FCSTD DOCUMENT  (FreeCAD 0.18.4R)
Label: carro-impresso
License: All rights reserved
LicenseURL: http://en.wikipedia.org/wiki/All_rights_reserved
objects: Sketcher::SketchObject×1, PartDesign::Body×1
note: 2 computed .brp shape members not serialized (recipe doc carries the construction recipe); baked Part::Feature solids carry a one-line shape summary decoded from their .brp

FEATURE [Sketcher::SketchObject] Sketch
  MapMode = 5
  Support = -> [XY_Plane]
  sketch-geometry (35):
    g0: LineSegment StartX=-22.5 StartY=-27.5 StartZ=0 EndX=22.5 EndY=-27.5 EndZ=0
    g1: LineSegment StartX=27.5 StartY=-22.5 StartZ=0 EndX=27.5 EndY=22.5 EndZ=0
    g2: LineSegment StartX=22.5 StartY=27.5 StartZ=0 EndX=-22.5 EndY=27.5 EndZ=0
    g3: LineSegment StartX=-27.5 StartY=22.5 StartZ=0 EndX=-27.5 EndY=-22.5 EndZ=0
    g4: ArcOfCircle CenterX=22.5 CenterY=22.5 CenterZ=0 NormalX=0 NormalY=0 NormalZ=1 AngleXU=0 Radius=5 StartAngle=0 EndAngle=1.5708
    g5: ArcOfCircle CenterX=-22.5 CenterY=22.5 CenterZ=0 NormalX=0 NormalY=0 NormalZ=1 AngleXU=0 Radius=5 StartAngle=1.5708 EndAngle=3.14159
    g6: ArcOfCircle CenterX=-22.5 CenterY=-22.5 CenterZ=0 NormalX=0 NormalY=0 NormalZ=1 AngleXU=0 Radius=5 StartAngle=3.14159 EndAngle=4.71239
    g7: ArcOfCircle CenterX=22.5 CenterY=-22.5 CenterZ=0 NormalX=0 NormalY=0 NormalZ=1 AngleXU=0 Radius=5 StartAngle=4.71239 EndAngle=6.28319
    g8: Circle CenterX=-20 CenterY=20 CenterZ=0 NormalX=0 NormalY=0 NormalZ=1 AngleXU=0 Radius=3
    g9: Circle CenterX=20 CenterY=20 CenterZ=0 NormalX=0 NormalY=0 NormalZ=1 AngleXU=0 Radius=3
    g10: Circle CenterX=0 CenterY=-20 CenterZ=0 NormalX=0 NormalY=0 NormalZ=1 AngleXU=0 Radius=3
    g11: LineSegment [constr] StartX=-27.5 StartY=20 StartZ=0 EndX=27.5 EndY=20 EndZ=0
    g12: Circle CenterX=20 CenterY=-20 CenterZ=0 NormalX=0 NormalY=0 NormalZ=1 AngleXU=0 Radius=1.5
    g13: Circle CenterX=20 CenterY=0 CenterZ=0 NormalX=0 NormalY=0 NormalZ=1 AngleXU=0 Radius=1.5
    g14: Circle CenterX=10 CenterY=20 CenterZ=0 NormalX=0 NormalY=0 NormalZ=1 AngleXU=0 Radius=1.5
    g15: Circle CenterX=10 CenterY=0 CenterZ=0 NormalX=0 NormalY=0 NormalZ=1 AngleXU=0 Radius=1.5
    g16: Circle CenterX=-10 CenterY=20 CenterZ=0 NormalX=0 NormalY=0 NormalZ=1 AngleXU=0 Radius=1.5
    g17: Circle CenterX=-10 CenterY=0 CenterZ=0 NormalX=0 NormalY=0 NormalZ=1 AngleXU=0 Radius=1.5
    g18: Circle CenterX=-20 CenterY=-20 CenterZ=0 NormalX=0 NormalY=0 NormalZ=1 AngleXU=0 Radius=1.5
    g19: Circle CenterX=-20 CenterY=0 CenterZ=0 NormalX=0 NormalY=0 NormalZ=1 AngleXU=0 Radius=1.5
    g20: LineSegment [constr] StartX=-10 StartY=27.5 StartZ=0 EndX=-10 EndY=-27.5 EndZ=0
    g21: LineSegment [constr] StartX=-20 StartY=27.5 StartZ=0 EndX=-20 EndY=-27.5 EndZ=0
    g22: LineSegment [constr] StartX=-27.5 StartY=-20 StartZ=0 EndX=27.5 EndY=-20 EndZ=0
    g23: LineSegment [constr] StartX=10 StartY=27.5 StartZ=0 EndX=10 EndY=-27.5 EndZ=0
    g24: LineSegment [constr] StartX=20 StartY=27.5 StartZ=0 EndX=20 EndY=-27.5 EndZ=0
    g25: LineSegment [constr] StartX=-27.5 StartY=-10 StartZ=0 EndX=27.5 EndY=-10 EndZ=0
    g26: LineSegment [constr] StartX=-27.5 StartY=10 StartZ=0 EndX=27.5 EndY=10 EndZ=0
    g27: Circle CenterX=-20 CenterY=10 CenterZ=0 NormalX=0 NormalY=0 NormalZ=1 AngleXU=0 Radius=1.5
    g28: Circle CenterX=-10 CenterY=10 CenterZ=0 NormalX=0 NormalY=0 NormalZ=1 AngleXU=0 Radius=1.5
    g29: Circle CenterX=10 CenterY=10 CenterZ=0 NormalX=0 NormalY=0 NormalZ=1 AngleXU=0 Radius=1.5
    g30: Circle CenterX=20 CenterY=10 CenterZ=0 NormalX=0 NormalY=0 NormalZ=1 AngleXU=0 Radius=1.5
    g31: Circle CenterX=10 CenterY=-10 CenterZ=0 NormalX=0 NormalY=0 NormalZ=1 AngleXU=0 Radius=1.5
    g32: Circle CenterX=-10 CenterY=-10 CenterZ=0 NormalX=0 NormalY=0 NormalZ=1 AngleXU=0 Radius=1.5
    g33: Circle CenterX=-20 CenterY=-10 CenterZ=0 NormalX=0 NormalY=0 NormalZ=1 AngleXU=0 Radius=1.5
    g34: Circle CenterX=20 CenterY=-10 CenterZ=0 NormalX=0 NormalY=0 NormalZ=1 AngleXU=0 Radius=1.5
  constraints (100):
    c: Horizontal(g0)
    c: Horizontal(g2)
    c: Vertical(g1)
    c: Vertical(g3)
    c: Tangent(g2,g4) = -1.5708
    c: Tangent(g1,g4) = -1.5708
    c: Tangent(g2,g5) = -1.5708
    c: Tangent(g3,g5) = -1.5708
    c: Tangent(g3,g6) = -1.5708
    c: Tangent(g0,g6) = -1.5708
    c: Tangent(g1,g7) = -1.5708
    c: Tangent(g0,g7) = -1.5708
    c: Equal(g5,g6)
    c: Equal(g6,g7)
    c: Equal(g7,g4)
    c: Symmetric(g7,g5,g-1)
    c: DistanceX(g3,g1) = 55
    c: DistanceY(g0,g2) = 55
    c: Diameter(g5) = 10
    c: PointOnObject(g10,g-2)
    c: Diameter(g10) = 6
    c: Diameter(g8) = 6
    c: Diameter(g9) = 6
    c: Horizontal(g11)
    c: PointOnObject(g8,g11)
    c: PointOnObject(g9,g11)
    c: PointOnObject(g11,g3)
    c: PointOnObject(g11,g1)
    c: DistanceY(g10,g11) = 40
    c: DistanceY(g10,g-1) = 20
    c: DistanceX(g8,g9) = 40
    c: DistanceX(g8,g-1) = 20
    c: PointOnObject(g13,g-1)
    c: PointOnObject(g14,g11)
    c: PointOnObject(g15,g-1)
    c: PointOnObject(g16,g11)
    c: PointOnObject(g17,g-1)
    c: PointOnObject(g19,g-1)
    c: Equal(g19,g17)
    c: Equal(g15,g13)
    c: Equal(g13,g14)
    c: Equal(g16,g18)
    c: Diameter(g16) = 3
    c: Vertical(g20)
    c: PointOnObject(g16,g20)
    c: PointOnObject(g17,g20)
    c: Vertical(g21)
    c: PointOnObject(g8,g21)
    c: PointOnObject(g19,g21)
    c: PointOnObject(g18,g21)
    c: Horizontal(g22)
    c: Vertical(g23)
    c: Vertical(g24)
    c: PointOnObject(g9,g24)
    c: PointOnObject(g13,g24)
    c: PointOnObject(g12,g22)
    c: PointOnObject(g10,g22)
    c: PointOnObject(g18,g22)
    c: PointOnObject(g12,g24)
    c: PointOnObject(g15,g23)
    c: PointOnObject(g14,g23)
    c: PointOnObject(g22,g1)
    c: PointOnObject(g22,g3)
    c: PointOnObject(g21,g0)
    c: PointOnObject(g21,g2)
    c: PointOnObject(g20,g2)
    c: PointOnObject(g23,g2)
    c: PointOnObject(g24,g2)
    c: PointOnObject(g20,g0)
    c: PointOnObject(g23,g0)
    c: PointOnObject(g24,g0)
    c: PointOnObject(g25,g3)
    c: PointOnObject(g25,g1)
    c: Horizontal(g25)
    c: DistanceY(g10,g25) = 10
    c: PointOnObject(g26,g3)
    c: PointOnObject(g26,g1)
    c: Horizontal(g26)
    c: PointOnObject(g27,g26)
    c: PointOnObject(g28,g26)
    c: PointOnObject(g29,g26)
    c: PointOnObject(g30,g26)
    c: PointOnObject(g31,g25)
    c: PointOnObject(g32,g25)
    c: PointOnObject(g33,g25)
    c: Equal(g27,g28)
    c: Equal(g29,g30)
    c: Equal(g31,g32)
    c: Equal(g32,g33)
    c: Equal(g33,g19)
    c: PointOnObject(g27,g21)
    c: PointOnObject(g28,g20)
    c: PointOnObject(g29,g23)
    c: PointOnObject(g30,g24)
    c: PointOnObject(g33,g21)
    c: PointOnObject(g32,g20)
    c: PointOnObject(g31,g23)
    c: PointOnObject(g34,g25)
    c: Equal(g34,g31)
    c: PointOnObject(g34,g24)
FEATURE [PartDesign::Body] Body
  Group = -> [Sketch]
  Origin = -> Origin
